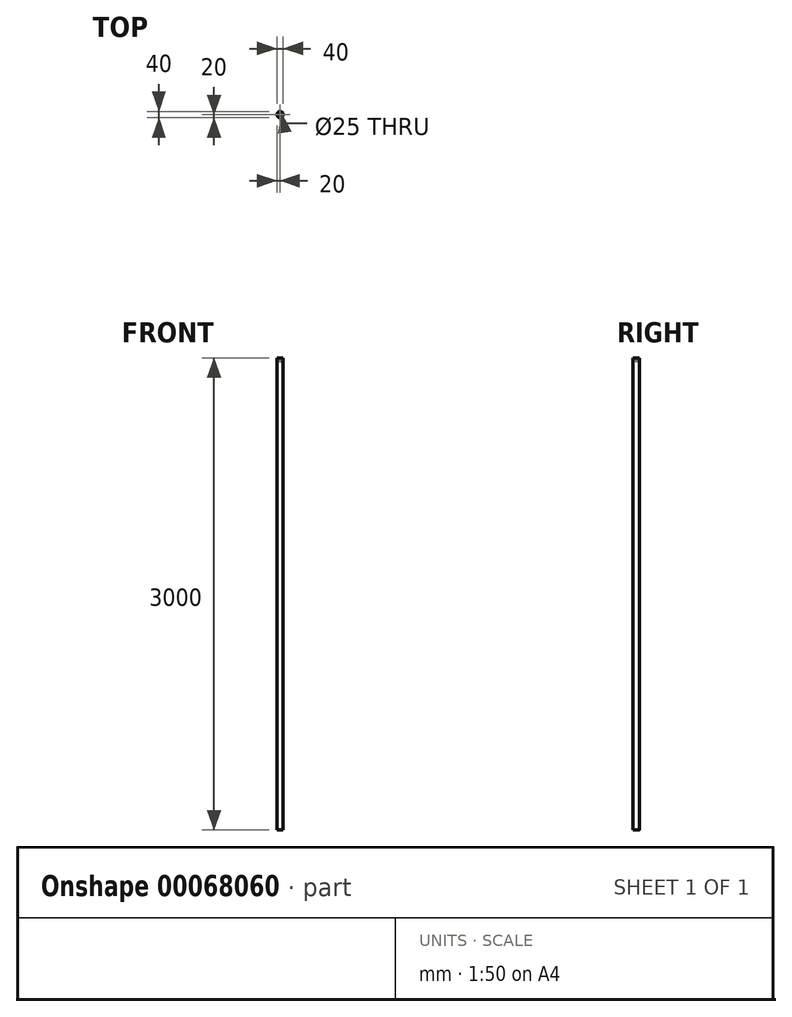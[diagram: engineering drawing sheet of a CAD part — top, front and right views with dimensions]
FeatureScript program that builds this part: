
annotation { "Feature Type Name" : "Feature", "Feature Type Description" : "" }
export const myFeature = defineFeature(function(context is Context, id is Id, definition is map)
    precondition{}
    {
        {
            var Q0;
            Q0=qCreatedBy(makeId("Top.planeOp"),FACE);
            var sketch = newSketch(context, id + "F0", { "sketchPlane" : qUnion([Q0])});
            skCircle(sketch, "E0", {"center": v(0, 0) * mm, "radius": 20 * mm});
            skSolve(sketch);
        }
        {
            var Q0;
            Q0=makeQuery(id+"F0.imprint","IMPRINT",FACE,{"disambiguationData":[TD([[makeQuery(id+"F0.imprint","IMPRINT",EDGE,{"derivedFrom":sQuery(id+"F0.wireOp",EDGE,"E0")}),1.0]])]});
            extrude(context, id + "F1", {"entities" : qUnion([Q0]), "depth" : 3000 * mm});
        }
        {
            var Q0;
            Q0=makeQuery(id+"F1.opExtrude","CAP_FACE",FACE,{"disambiguationData":[OSD([sQuery(id+"F0.wireOp",EDGE,"E0")])],"isStart":false});
            var sketch = newSketch(context, id + "F2", { "sketchPlane" : qUnion([Q0])});
            skCircle(sketch, "E1", {"center": v(0, 0) * mm, "radius": 11.26 * mm});
            skSolve(sketch);
        }
        {
            var Q0;
            Q0=sQuery(id+"F2.wireOp",VERTEX,"E1.center");
            var Q1;
            Q1=makeQuery(id+"F1.opExtrude","SWEPT_BODY",BODY,{"disambiguationData":[OSD([sQuery(id+"F0.wireOp",EDGE,"E0")])]});
            hole(context, id + "F3", {"style" : HoleStyle.SIMPLE, "holeDiameter" : 25 * mm, "endStyle" : HoleEndStyle.BLIND, "holeDepth" : 18 * mm, "locations" : qUnion([Q0]), "scope" : qUnion([Q1])});
        }
        {
            var Q0;
            Q0=qCreatedBy(makeId("Front.planeOp"),FACE);
            cPlane(context, id + "F4", {"entities" : qUnion([Q0]), "cplaneType" : CPlaneType.OFFSET, "offset" : 20 * mm, "oppositeDirection" : true, "width" : 150 * mm, "height" : 150 * mm});
        }
    });
